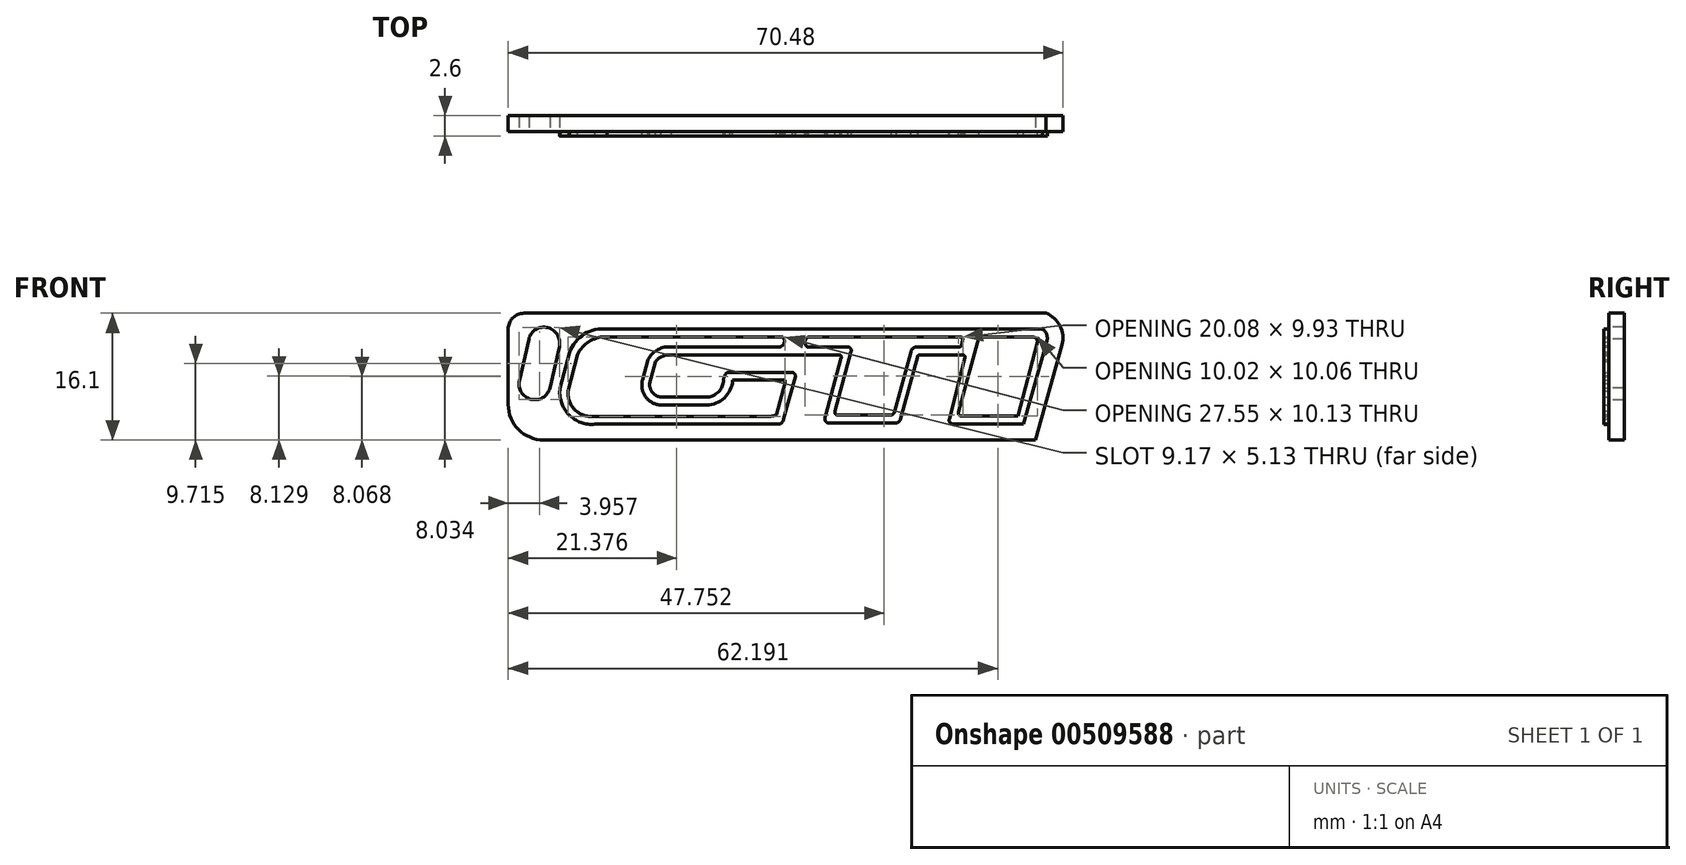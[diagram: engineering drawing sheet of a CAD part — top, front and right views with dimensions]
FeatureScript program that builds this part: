
annotation { "Feature Type Name" : "Feature", "Feature Type Description" : "" }
export const myFeature = defineFeature(function(context is Context, id is Id, definition is map)
    precondition{}
    {
        {
            var Q0;
            Q0=qCreatedBy(makeId("Front.planeOp"),FACE);
            var sketch = newSketch(context, id + "F0", { "sketchPlane" : qUnion([Q0])});
            skLineSegment(sketch, "E0.bottom", {"start": v(-46.02, 4.2) * mm, "end": v(43.98, 4.2) * mm});
            skLineSegment(sketch, "E0.top", {"start": v(-46.02, 24.2) * mm, "end": v(43.98, 24.2) * mm});
            skLineSegment(sketch, "E0.left", {"start": v(-46.02, 4.2) * mm, "end": v(-46.02, 24.2) * mm});
            skLineSegment(sketch, "E0.right", {"start": v(43.98, 4.2) * mm, "end": v(43.98, 24.2) * mm});
            skSolve(sketch);
        }
        {
            var Q0;
            Q0 = qSketchRegion(id + "F0", true);
            extrude(context, id + "F1", {"entities" : qUnion([Q0]), "depth" : 2 * mm, "offsetDistance" : 25 * mm});
        }
        {
            var Q0;
            Q0=makeQuery(id+"F1.opExtrude","CAP_FACE",FACE,{"disambiguationData":[OSD([sQuery(id+"F0.wireOp",EDGE,"E0.bottom"),sQuery(id+"F0.wireOp",EDGE,"E0.top"),sQuery(id+"F0.wireOp",EDGE,"E0.left"),sQuery(id+"F0.wireOp",EDGE,"E0.right")])],"isStart":false});
            var sketch = newSketch(context, id + "F2", { "sketchPlane" : qUnion([Q0])});
            skLineSegment(sketch, "E1", {"start": v(-14.78, 18.36) * mm, "end": v(40.51, 18.36) * mm});
            skLineSegment(sketch, "E2", {"start": v(41.09, 16.85) * mm, "end": v(38.13, 6.3) * mm});
            skLineSegment(sketch, "E3", {"start": v(38.13, 6.3) * mm, "end": v(29.14, 6.3) * mm});
            skLineSegment(sketch, "E4", {"start": v(32.45, 17.36) * mm, "end": v(29.85, 7.8) * mm});
            skLineSegment(sketch, "E5", {"start": v(30.18, 7.3) * mm, "end": v(37.4, 7.3) * mm});
            skLineSegment(sketch, "E6", {"start": v(37.4, 7.3) * mm, "end": v(39.86, 16.7) * mm});
            skLineSegment(sketch, "E7", {"start": v(32.45, 17.36) * mm, "end": v(39.26, 17.36) * mm});
            skLineSegment(sketch, "E8", {"start": v(-18.52, 15.11) * mm, "end": v(-19.74, 10.5) * mm});
            skLineSegment(sketch, "E9", {"start": v(-19.56, 15.4) * mm, "end": v(-20.76, 10.85) * mm});
            skLineSegment(sketch, "E10", {"start": v(-16.31, 7.26) * mm, "end": v(5.89, 7.26) * mm});
            skLineSegment(sketch, "E11", {"start": v(7.23, 6.26) * mm, "end": v(-16.31, 6.26) * mm});
            skLineSegment(sketch, "E12", {"start": v(7.65, 6.9) * mm, "end": v(9.13, 12.3) * mm});
            skLineSegment(sketch, "E13", {"start": v(7.79, 11.48) * mm, "end": v(6.77, 7.5) * mm});
            skLineSegment(sketch, "E14", {"start": v(8.76, 12.85) * mm, "end": v(0.84, 12.85) * mm});
            skLineSegment(sketch, "E15", {"start": v(1.18, 11.85) * mm, "end": v(7.79, 11.85) * mm});
            skLineSegment(sketch, "E16", {"start": v(-7.79, 9.7) * mm, "end": v(-2.21, 9.7) * mm});
            skLineSegment(sketch, "E17", {"start": v(-2.18, 8.7) * mm, "end": v(-7.92, 8.7) * mm});
            skLineSegment(sketch, "E18", {"start": v(10.8, 17.36) * mm, "end": v(30.05, 17.36) * mm});
            skLineSegment(sketch, "E19", {"start": v(30.17, 15.07) * mm, "end": v(24.99, 15.07) * mm});
            skLineSegment(sketch, "E20", {"start": v(13.22, 6.42) * mm, "end": v(22, 6.42) * mm});
            skLineSegment(sketch, "E21", {"start": v(10.64, 16.08) * mm, "end": v(15.82, 16.08) * mm});
            skLineSegment(sketch, "E22", {"start": v(24.72, 14.99) * mm, "end": v(22.52, 6.95) * mm});
            skLineSegment(sketch, "E23", {"start": v(29.91, 16.07) * mm, "end": v(24.54, 16.07) * mm});
            skLineSegment(sketch, "E24", {"start": v(7.18, 16.08) * mm, "end": v(-6.59, 16.08) * mm});
            skLineSegment(sketch, "E25", {"start": v(14.79, 15.08) * mm, "end": v(-6.86, 15.08) * mm});
            skLineSegment(sketch, "E26", {"start": v(-8.61, 14.24) * mm, "end": v(-9.37, 11.4) * mm});
            skLineSegment(sketch, "E27", {"start": v(14.96, 14.66) * mm, "end": v(12.98, 7.31) * mm});
            skLineSegment(sketch, "E28", {"start": v(16.22, 15.5) * mm, "end": v(14.18, 7.94) * mm});
            skLineSegment(sketch, "E29", {"start": v(23.8, 15.42) * mm, "end": v(21.72, 7.81) * mm});
            skLineSegment(sketch, "E30", {"start": v(21.34, 7.42) * mm, "end": v(14.51, 7.42) * mm});
            skLineSegment(sketch, "E31", {"start": v(7.53, 17.36) * mm, "end": v(-15.03, 17.36) * mm});
            skLineSegment(sketch, "E32", {"start": v(-9.6, 14.48) * mm, "end": v(-10.28, 11.88) * mm});
            skArc(sketch, "E33", {"start": v(-14.78, 18.36) * mm, "mid": v(-17.68, 17.7) * mm, "end": v(-19.56, 15.4) * mm});
            skArc(sketch, "E34", {"start": v(-15.03, 17.36) * mm, "mid": v(-17.1, 16.75) * mm, "end": v(-18.52, 15.11) * mm});
            skArc(sketch, "E35", {"start": v(-6.59, 16.08) * mm, "mid": v(-8.33, 15.74) * mm, "end": v(-9.6, 14.48) * mm});
            skArc(sketch, "E36", {"start": v(-6.86, 15.08) * mm, "mid": v(-7.83, 14.86) * mm, "end": v(-8.61, 14.24) * mm});
            skArc(sketch, "E37", {"start": v(16.22, 15.5) * mm, "mid": v(16.16, 15.88) * mm, "end": v(15.82, 16.08) * mm});
            skArc(sketch, "E38", {"start": v(14.96, 14.66) * mm, "mid": v(14.95, 14.9) * mm, "end": v(14.79, 15.08) * mm});
            skArc(sketch, "E39", {"start": v(10.8, 17.36) * mm, "mid": v(10.37, 16.76) * mm, "end": v(10.64, 16.08) * mm});
            skArc(sketch, "E40", {"start": v(7.18, 16.08) * mm, "mid": v(7.72, 16.62) * mm, "end": v(7.53, 17.36) * mm});
            skArc(sketch, "E41", {"start": v(-19.74, 10.5) * mm, "mid": v(-18.82, 8.04) * mm, "end": v(-16.31, 7.26) * mm});
            skArc(sketch, "E42", {"start": v(-20.76, 10.85) * mm, "mid": v(-19.65, 7.48) * mm, "end": v(-16.31, 6.26) * mm});
            skArc(sketch, "E43", {"start": v(7.23, 6.26) * mm, "mid": v(7.5, 6.55) * mm, "end": v(7.65, 6.9) * mm});
            skArc(sketch, "E44", {"start": v(5.89, 7.26) * mm, "mid": v(6.34, 7.32) * mm, "end": v(6.77, 7.5) * mm});
            skArc(sketch, "E45", {"start": v(14.18, 7.94) * mm, "mid": v(14.2, 7.59) * mm, "end": v(14.51, 7.42) * mm});
            skArc(sketch, "E46", {"start": v(12.98, 7.31) * mm, "mid": v(12.9, 6.81) * mm, "end": v(13.22, 6.42) * mm});
            skArc(sketch, "E47", {"start": v(-2.21, 9.7) * mm, "mid": v(-0.66, 10.34) * mm, "end": v(0, 11.9) * mm});
            skArc(sketch, "E48", {"start": v(-2.18, 8.7) * mm, "mid": v(0.12, 9.61) * mm, "end": v(1.18, 11.85) * mm});
            skArc(sketch, "E49", {"start": v(0.18, 12.44) * mm, "mid": v(0.07, 12.17) * mm, "end": v(0, 11.9) * mm});
            skArc(sketch, "E50", {"start": v(0.84, 12.85) * mm, "mid": v(0.43, 12.78) * mm, "end": v(0.18, 12.44) * mm});
            skArc(sketch, "E51", {"start": v(21.34, 7.42) * mm, "mid": v(21.58, 7.57) * mm, "end": v(21.72, 7.81) * mm});
            skArc(sketch, "E52", {"start": v(22, 6.42) * mm, "mid": v(22.33, 6.62) * mm, "end": v(22.52, 6.95) * mm});
            skArc(sketch, "E53", {"start": v(29.85, 7.8) * mm, "mid": v(29.9, 7.48) * mm, "end": v(30.18, 7.3) * mm});
            skArc(sketch, "E54", {"start": v(28.7, 6.96) * mm, "mid": v(28.75, 6.51) * mm, "end": v(29.14, 6.3) * mm});
            skArc(sketch, "E55", {"start": v(24.54, 16.07) * mm, "mid": v(24.05, 15.88) * mm, "end": v(23.8, 15.42) * mm});
            skArc(sketch, "E56", {"start": v(24.99, 15.07) * mm, "mid": v(24.85, 15.05) * mm, "end": v(24.72, 14.99) * mm});
            skArc(sketch, "E57", {"start": v(30.45, 17.2) * mm, "mid": v(30.27, 17.31) * mm, "end": v(30.05, 17.36) * mm});
            skArc(sketch, "E58", {"start": v(29.91, 16.07) * mm, "mid": v(30.1, 16.12) * mm, "end": v(30.24, 16.25) * mm});
            skLineSegment(sketch, "E59", {"start": v(30.45, 17.2) * mm, "end": v(30.24, 16.25) * mm});
            skLineSegment(sketch, "E60", {"start": v(30.68, 14.73) * mm, "end": v(28.7, 6.96) * mm});
            skArc(sketch, "E61", {"start": v(30.68, 14.73) * mm, "mid": v(30.64, 14.95) * mm, "end": v(30.45, 15.07) * mm});
            skLineSegment(sketch, "E62", {"start": v(30.45, 15.07) * mm, "end": v(30.17, 15.07) * mm});
            skArc(sketch, "E63", {"start": v(39.86, 16.7) * mm, "mid": v(39.7, 17.16) * mm, "end": v(39.26, 17.36) * mm});
            skArc(sketch, "E64", {"start": v(41.09, 16.85) * mm, "mid": v(41.05, 17.7) * mm, "end": v(40.51, 18.36) * mm});
            skArc(sketch, "E65", {"start": v(-9.37, 11.4) * mm, "mid": v(-8.95, 10.2) * mm, "end": v(-7.79, 9.7) * mm});
            skArc(sketch, "E66", {"start": v(-10.28, 11.88) * mm, "mid": v(-9.87, 9.71) * mm, "end": v(-7.92, 8.7) * mm});
            skArc(sketch, "E67", {"start": v(9.13, 12.3) * mm, "mid": v(9.05, 12.65) * mm, "end": v(8.76, 12.85) * mm});
            skArc(sketch, "E68", {"start": v(7.79, 11.48) * mm, "mid": v(7.81, 11.66) * mm, "end": v(7.79, 11.85) * mm});
            skSolve(sketch);
        }
        {
            var Q0;
            Q0=makeQuery(id+"F2.imprint","IMPRINT",FACE,{"disambiguationData":[TD([[makeQuery(id+"F2.imprint","IMPRINT",EDGE,{"derivedFrom":sQuery(id+"F2.wireOp",EDGE,"E1")}),-1.0]])]});
            extrude(context, id + "F3", {"entities" : qUnion([Q0]), "depth" : .6 * mm, "offsetDistance" : 25 * mm});
        }
        {
            var Q0;
            Q0=makeQuery(id+"F1.opExtrude","CAP_FACE",FACE,{"disambiguationData":[OSD([sQuery(id+"F0.wireOp",EDGE,"E0.bottom"),sQuery(id+"F0.wireOp",EDGE,"E0.top"),sQuery(id+"F0.wireOp",EDGE,"E0.left"),sQuery(id+"F0.wireOp",EDGE,"E0.right")])],"isStart":false});
            var sketch = newSketch(context, id + "F4", { "sketchPlane" : qUnion([Q0])});
            skLineSegment(sketch, "E69.0", {"start": v(43.01, 16.31) * mm, "end": v(39.64, 4.26) * mm});
            skArc(sketch, "E69.1", {"start": v(43.01, 16.31) * mm, "mid": v(42.77, 18.74) * mm, "end": v(40.96, 20.36) * mm});
            skLineSegment(sketch, "E69.2", {"start": v(-25.34, 20.36) * mm, "end": v(40.96, 20.36) * mm});
            skLineSegment(sketch, "E69.3", {"start": v(39.64, 4.26) * mm, "end": v(-22.84, 4.26) * mm});
            skLineSegment(sketch, "E70", {"start": v(-27.34, 18.36) * mm, "end": v(-27.34, 8.76) * mm});
            skPoint(sketch, "E71.orphan", {"position": v(-14.68, 20.36) * mm});
            skArc(sketch, "E72", {"start": v(-20.84, 16.14) * mm, "mid": v(-22.31, 18.52) * mm, "end": v(-24.72, 17.1) * mm});
            skPoint(sketch, "E73.visualSharp", {"position": v(-27.34, 4.26) * mm});
            skArc(sketch, "E73.filletArc", {"start": v(-27.34, 8.76) * mm, "mid": v(-26.03, 5.58) * mm, "end": v(-22.84, 4.26) * mm});
            skPoint(sketch, "E74.visualSharp", {"position": v(-27.34, 20.36) * mm});
            skArc(sketch, "E74.filletArc", {"start": v(-25.34, 20.36) * mm, "mid": v(-26.76, 19.77) * mm, "end": v(-27.34, 18.36) * mm});
            skArc(sketch, "E75", {"start": v(-25.92, 11.81) * mm, "mid": v(-24.46, 9.43) * mm, "end": v(-22.05, 10.84) * mm});
            skLineSegment(sketch, "E76", {"start": v(-22.05, 10.84) * mm, "end": v(-20.84, 16.14) * mm});
            skLineSegment(sketch, "E77", {"start": v(-24.72, 17.1) * mm, "end": v(-25.92, 11.81) * mm});
            skLineSegment(sketch, "E78.bottom", {"start": v(-47.44, 27.68) * mm, "end": v(46, 27.68) * mm});
            skLineSegment(sketch, "E78.top", {"start": v(-47.44, -7.5) * mm, "end": v(46, -7.5) * mm});
            skLineSegment(sketch, "E78.left", {"start": v(-47.44, 27.68) * mm, "end": v(-47.44, -7.5) * mm});
            skLineSegment(sketch, "E78.right", {"start": v(46, 27.68) * mm, "end": v(46, -7.5) * mm});
            skSolve(sketch);
        }
        {
            var Q0;
            Q0=makeQuery(id+"F4.imprint","IMPRINT",FACE,{"disambiguationData":[TD([[makeQuery(id+"F4.imprint","IMPRINT",EDGE,{"derivedFrom":sQuery(id+"F4.wireOp",EDGE,"E69.0")}),1.0]])]});
            var Q1;
            Q1=makeQuery(id+"F4.imprint","IMPRINT",FACE,{"disambiguationData":[TD([[makeQuery(id+"F4.imprint","IMPRINT",EDGE,{"derivedFrom":sQuery(id+"F4.wireOp",EDGE,"E72")}),1.0]])]});
            extrude(context, id + "F5", {"entities" : qUnion([Q0, Q1]), "operationType" : NewBodyOperationType.REMOVE, "endBound" : BoundingType.SYMMETRIC, "oppositeDirection" : true, "depth" : 25 * mm, "offsetDistance" : 25 * mm});
        }
    });
